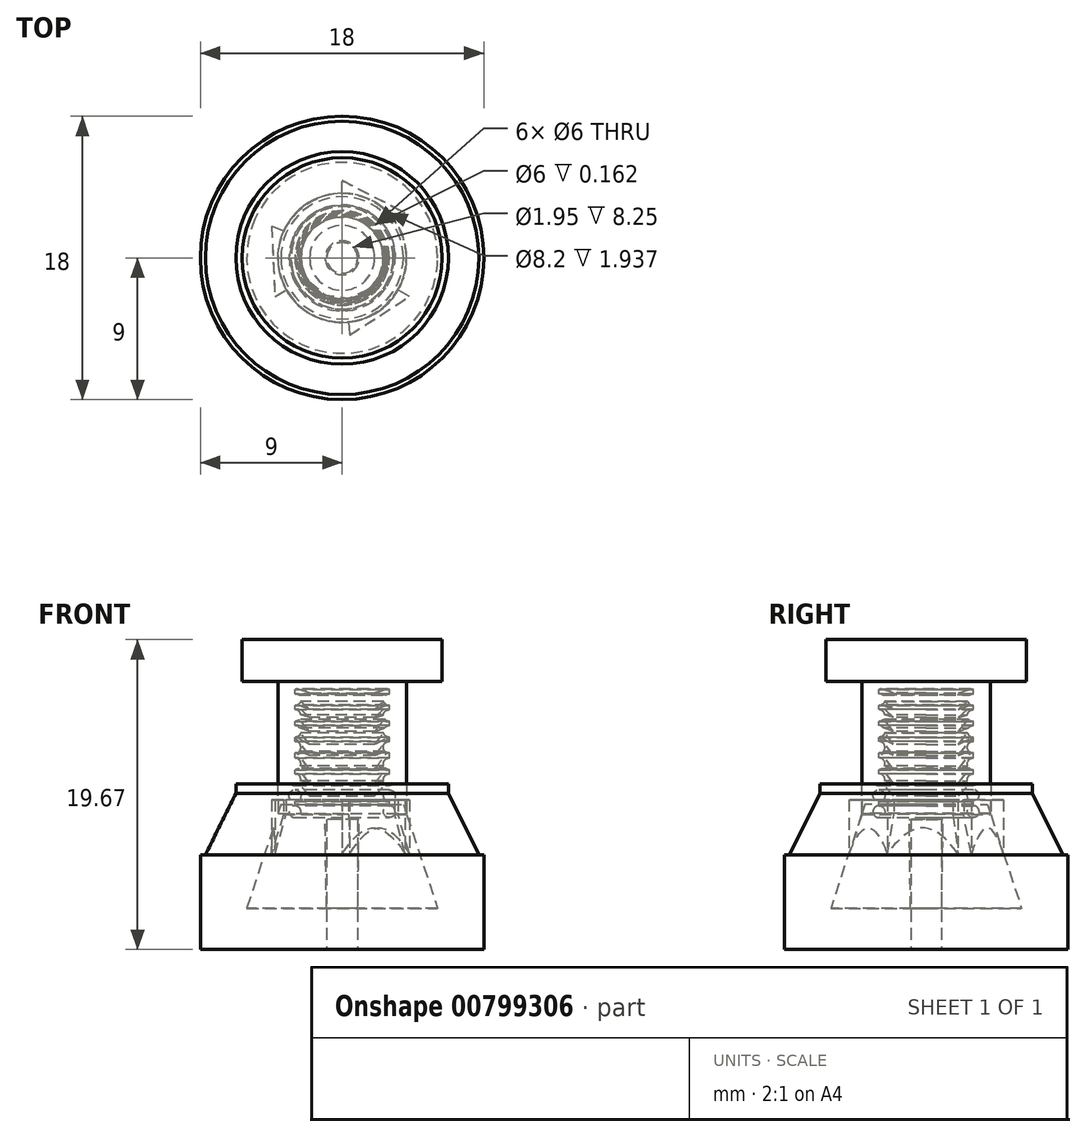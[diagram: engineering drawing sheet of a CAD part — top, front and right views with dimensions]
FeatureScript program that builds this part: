
annotation { "Feature Type Name" : "Feature", "Feature Type Description" : "" }
export const myFeature = defineFeature(function(context is Context, id is Id, definition is map)
    precondition{}
    {
        {
            var Q0;
            Q0=qCreatedBy(makeId("Top.planeOp"),FACE);
            var sketch = newSketch(context, id + "F0", { "sketchPlane" : qUnion([Q0])});
            skCircle(sketch, "E0", {"center": v(0, 0) * mm, "radius": 4.08 * mm});
            skSolve(sketch);
        }
        {
            var Q0;
            Q0=makeQuery(id+"F0.imprint","IMPRINT",FACE,{"disambiguationData":[TD([[makeQuery(id+"F0.imprint","IMPRINT",EDGE,{"derivedFrom":sQuery(id+"F0.wireOp",EDGE,"E0")}),1.0]])]});
            extrude(context, id + "F1", {"entities" : qUnion([Q0]), "depth" : 13 * mm, "offsetDistance" : 25 * mm});
        }
        {
            var Q0;
            Q0=qCreatedBy(makeId("Top.planeOp"),FACE);
            var sketch = newSketch(context, id + "F2", { "sketchPlane" : qUnion([Q0])});
            skCircle(sketch, "E1", {"center": v(0, 0) * mm, "radius": 9 * mm});
            skSolve(sketch);
        }
        {
            var Q0;
            Q0=makeQuery(id+"F2.imprint","IMPRINT",FACE,{"disambiguationData":[TD([[makeQuery(id+"F2.imprint","IMPRINT",EDGE,{"derivedFrom":sQuery(id+"F2.wireOp",EDGE,"E1")}),1.0]])]});
            extrude(context, id + "F3", {"entities" : qUnion([Q0]), "operationType" : NewBodyOperationType.ADD, "depth" : 3 * mm, "offsetDistance" : 25 * mm});
        }
        {
            var Q0;
            Q0=qCreatedBy(makeId("Top.planeOp"),FACE);
            var sketch = newSketch(context, id + "F4", { "sketchPlane" : qUnion([Q0])});
            skLineSegment(sketch, "E2", {"start": v(0, 0) * mm, "end": v(0, 10.37) * mm, "construction": true});
            skLineSegment(sketch, "E3", {"start": v(0, 0) * mm, "end": v(10.66, -6.15) * mm, "construction": true});
            skLineSegment(sketch, "E4", {"start": v(0, 0) * mm, "end": v(-9.47, -5.47) * mm, "construction": true});
            skCircle(sketch, "E5", {"center": v(0, 0) * mm, "radius": 4.92 * mm, "construction": true});
            skLineSegment(sketch, "E6", {"start": v(0, 0) * mm, "end": v(4, 2.87) * mm});
            skLineSegment(sketch, "E7", {"start": v(4, 2.87) * mm, "end": v(0, 4.92) * mm});
            skLineSegment(sketch, "E8", {"start": v(0, 4.92) * mm, "end": v(0, 0) * mm});
            skLineSegment(sketch, "E9", {"start": v(0, 0) * mm, "end": v(4.27, -2.46) * mm});
            skLineSegment(sketch, "E10", {"start": v(4.27, -2.46) * mm, "end": v(0.48, -4.9) * mm});
            skLineSegment(sketch, "E11", {"start": v(0.48, -4.9) * mm, "end": v(0, 0) * mm});
            skLineSegment(sketch, "E12", {"start": v(0, 0) * mm, "end": v(-4.27, -2.46) * mm});
            skLineSegment(sketch, "E13", {"start": v(-4.27, -2.46) * mm, "end": v(-4.49, 2.03) * mm});
            skLineSegment(sketch, "E14", {"start": v(-4.49, 2.03) * mm, "end": v(0, 0) * mm});
            skSolve(sketch);
        }
        {
            var Q0;
            Q0 = qSketchRegion(id + "F4", true);
            extrude(context, id + "F5", {"entities" : qUnion([Q0]), "operationType" : NewBodyOperationType.ADD, "depth" : 5 * mm, "offsetDistance" : 25 * mm});
        }
        {
            var Q0;
            Q0=qCreatedBy(makeId("Top.planeOp"),FACE);
            var sketch = newSketch(context, id + "F6", { "sketchPlane" : qUnion([Q0])});
            skCircle(sketch, "E15", {"center": v(0, 0) * mm, "radius": 0.97 * mm});
            skSolve(sketch);
        }
        {
            var Q0;
            Q0 = qSketchRegion(id + "F6", true);
            extrude(context, id + "F7", {"entities" : qUnion([Q0]), "operationType" : NewBodyOperationType.REMOVE, "endBound" : BoundingType.UP_TO_NEXT, "depth" : 25 * mm, "offsetDistance" : 25 * mm});
        }
        {
            var Q0;
            Q0=makeQuery(id+"F3.opExtrude","CAP_FACE",FACE,{"disambiguationData":[OSD([sQuery(id+"F2.wireOp",EDGE,"E1")])],"isStart":false});
            var sketch = newSketch(context, id + "F8", { "sketchPlane" : qUnion([Q0])});
            skCircle(sketch, "E16", {"center": v(0, 0) * mm, "radius": 9 * mm});
            skSolve(sketch);
        }
        {
            var Q0;
            Q0=makeQuery(id+"F8.imprint","IMPRINT",FACE,{"disambiguationData":[TD([[makeQuery(id+"F8.imprint","IMPRINT",EDGE,{"derivedFrom":sQuery(id+"F8.wireOp",EDGE,"E16")}),1.0]])]});
            extrude(context, id + "F9", {"entities" : qUnion([Q0]), "depth" : 3 * mm, "offsetDistance" : 25 * mm});
        }
        {
            var Q0;
            Q0=makeQuery(id+"F9.opExtrude","CAP_FACE",FACE,{"disambiguationData":[OSD([sQuery(id+"F0.wireOp",EDGE,"E0"),sQuery(id+"F2.wireOp",EDGE,"E1"),sQuery(id+"F4.wireOp",EDGE,"E6"),sQuery(id+"F4.wireOp",EDGE,"E7"),sQuery(id+"F4.wireOp",EDGE,"E8"),sQuery(id+"F4.wireOp",EDGE,"E9"),sQuery(id+"F4.wireOp",EDGE,"E10"),sQuery(id+"F4.wireOp",EDGE,"E11"),sQuery(id+"F4.wireOp",EDGE,"E12"),sQuery(id+"F4.wireOp",EDGE,"E13"),sQuery(id+"F4.wireOp",EDGE,"E14"),sQuery(id+"F8.wireOp",EDGE,"E16")])],"isStart":false});
            var sketch = newSketch(context, id + "F10", { "sketchPlane" : qUnion([Q0])});
            skCircle(sketch, "E17", {"center": v(0, 0) * mm, "radius": 6 * mm});
            skCircle(sketch, "E18", {"center": v(0, 0) * mm, "radius": 4.1 * mm});
            skSolve(sketch);
        }
        {
            var Q0;
            Q0=makeQuery(id+"F10.imprint","IMPRINT",FACE,{"disambiguationData":[TD([[makeQuery(id+"F10.imprint","IMPRINT",EDGE,{"derivedFrom":sQuery(id+"F10.wireOp",EDGE,"E17")}),1.0]])]});
            extrude(context, id + "F11", {"entities" : qUnion([Q0]), "operationType" : NewBodyOperationType.ADD, "depth" : 3.5 * mm, "offsetDistance" : 25 * mm});
        }
        {
            var Q0;
            Q0=makeQuery(id+"F11.opExtrude","CAP_FACE",FACE,{"disambiguationData":[OSD([sQuery(id+"F2.wireOp",EDGE,"E1"),sQuery(id+"F4.wireOp",EDGE,"E6"),sQuery(id+"F4.wireOp",EDGE,"E7"),sQuery(id+"F4.wireOp",EDGE,"E8"),sQuery(id+"F4.wireOp",EDGE,"E9"),sQuery(id+"F4.wireOp",EDGE,"E10"),sQuery(id+"F4.wireOp",EDGE,"E11"),sQuery(id+"F4.wireOp",EDGE,"E12"),sQuery(id+"F4.wireOp",EDGE,"E13"),sQuery(id+"F4.wireOp",EDGE,"E14"),sQuery(id+"F10.wireOp",EDGE,"E17"),sQuery(id+"F10.wireOp",EDGE,"E18")])],"isStart":false});
            var sketch = newSketch(context, id + "F12", { "sketchPlane" : qUnion([Q0])});
            skCircle(sketch, "E19", {"center": v(0, 0) * mm, "radius": 6.75 * mm});
            skSolve(sketch);
        }
        {
            var Q0;
            Q0 = qSketchRegion(id + "F12", true);
            extrude(context, id + "F13", {"entities" : qUnion([Q0]), "operationType" : NewBodyOperationType.ADD, "depth" : 1 * mm, "offsetDistance" : 25 * mm});
        }
        {
            var Q0;
            Q0=makeQuery(id+"F13.opExtrude","CAP_FACE",FACE,{"disambiguationData":[OSD([sQuery(id+"F12.wireOp",EDGE,"E19")])],"isStart":false});
            var sketch = newSketch(context, id + "F14", { "sketchPlane" : qUnion([Q0])});
            skCircle(sketch, "E20", {"center": v(0, 0) * mm, "radius": 4.1 * mm});
            skSolve(sketch);
        }
        {
            var Q0;
            Q0 = qSketchRegion(id + "F14", true);
            extrude(context, id + "F15", {"entities" : qUnion([Q0]), "operationType" : NewBodyOperationType.REMOVE, "oppositeDirection" : true, "depth" : 1 * mm, "offsetDistance" : 25 * mm});
        }
        {
            var Q0;
            Q0=qCreatedBy(makeId("Front.planeOp"),FACE);
            var sketch = newSketch(context, id + "F16", { "sketchPlane" : qUnion([Q0])});
            skLineSegment(sketch, "E21", {"start": v(0, 0) * mm, "end": v(0, 14.07) * mm, "construction": true});
            skLineSegment(sketch, "E22", {"start": v(-6.68, 10.05) * mm, "end": v(-8.74, 5.89) * mm});
            skLineSegment(sketch, "E23", {"start": v(-8.74, 5.89) * mm, "end": v(-5.87, 5.89) * mm});
            skLineSegment(sketch, "E24", {"start": v(-5.87, 5.89) * mm, "end": v(-5.87, 9.87) * mm});
            skLineSegment(sketch, "E25", {"start": v(-5.87, 9.87) * mm, "end": v(-6.68, 10.05) * mm});
            skSolve(sketch);
        }
        {
            var Q0;
            Q0=makeQuery(id+"F16.imprint","IMPRINT",FACE,{"disambiguationData":[TD([[makeQuery(id+"F16.imprint","IMPRINT",EDGE,{"derivedFrom":sQuery(id+"F16.wireOp",EDGE,"E22")}),1.0]])]});
            var Q1;
            Q1=sQuery(id+"F16.wireOp",EDGE,"E21");
            revolve(context, id + "F17", {"operationType" : NewBodyOperationType.ADD, "surfaceOperationType" : NewSurfaceOperationType.NEW, "entities" : qUnion([Q0]), "axis" : qUnion([Q1]), "revolveType" : RevolveType.FULL});
        }
        {
            var Q0;
            Q0=qCreatedBy(makeId("Front.planeOp"),FACE);
            var sketch = newSketch(context, id + "F18", { "sketchPlane" : qUnion([Q0])});
            skLineSegment(sketch, "E26", {"start": v(0, 0) * mm, "end": v(0, 10.64) * mm, "construction": true});
            skLineSegment(sketch, "E27", {"start": v(-3.88, 9.22) * mm, "end": v(-6.06, 2.61) * mm});
            skLineSegment(sketch, "E28", {"start": v(-6.06, 2.61) * mm, "end": v(-1, 2.61) * mm});
            skLineSegment(sketch, "E29", {"start": v(-1, 2.61) * mm, "end": v(-1.1, 9.22) * mm});
            skLineSegment(sketch, "E30", {"start": v(-1.1, 9.22) * mm, "end": v(-3.88, 9.22) * mm});
            skSolve(sketch);
        }
        {
            var Q0;
            Q0=makeQuery(id+"F18.imprint","IMPRINT",FACE,{"disambiguationData":[TD([[makeQuery(id+"F18.imprint","IMPRINT",EDGE,{"derivedFrom":sQuery(id+"F18.wireOp",EDGE,"E27")}),1.0]])]});
            var Q1;
            Q1=sQuery(id+"F18.wireOp",EDGE,"E26");
            revolve(context, id + "F19", {"operationType" : NewBodyOperationType.REMOVE, "surfaceOperationType" : NewSurfaceOperationType.NEW, "entities" : qUnion([Q0]), "axis" : qUnion([Q1]), "revolveType" : RevolveType.FULL, "oppositeDirection" : true});
        }
        {
            var Q0;
            Q0=makeQuery(id+"F1.opExtrude","CAP_FACE",FACE,{"disambiguationData":[OSD([sQuery(id+"F0.wireOp",EDGE,"E0")])],"isStart":false});
            var sketch = newSketch(context, id + "F20", { "sketchPlane" : qUnion([Q0])});
            skCircle(sketch, "E31", {"center": v(0, 0) * mm, "radius": 4.08 * mm});
            skSolve(sketch);
        }
        {
            var Q0;
            Q0 = qSketchRegion(id + "F20", true);
            extrude(context, id + "F21", {"entities" : qUnion([Q0]), "operationType" : NewBodyOperationType.ADD, "depth" : 4.25 * mm, "offsetDistance" : 25 * mm});
        }
        {
            var Q0;
            Q0=makeQuery(id+"F21.opExtrude","CAP_FACE",FACE,{"disambiguationData":[OSD([sQuery(id+"F20.wireOp",EDGE,"E31")])],"isStart":false});
            var sketch = newSketch(context, id + "F22", { "sketchPlane" : qUnion([Q0])});
            skCircle(sketch, "E32", {"center": v(0, 0) * mm, "radius": 3 * mm});
            skSolve(sketch);
        }
        {
            var Q0;
            Q0 = qSketchRegion(id + "F22", true);
            extrude(context, id + "F23", {"entities" : qUnion([Q0]), "operationType" : NewBodyOperationType.REMOVE, "oppositeDirection" : true, "depth" : 9 * mm, "offsetDistance" : 25 * mm});
        }
        {
            var Q0;
            Q0=qCreatedBy(makeId("Front.planeOp"),FACE);
            var sketch = newSketch(context, id + "F24", { "sketchPlane" : qUnion([Q0])});
            skLineSegment(sketch, "E33", {"start": v(0, 5.73) * mm, "end": v(0, 20.07) * mm, "construction": true});
            skLineSegment(sketch, "E34", {"start": v(1.15, 17.03) * mm, "end": v(-8.67, 17.03) * mm, "construction": true});
            skLineSegment(sketch, "E35", {"start": v(-3, 9.08) * mm, "end": v(-3, 20.34) * mm, "construction": true});
            skLineSegment(sketch, "E36", {"start": v(-2.06, 20.34) * mm, "end": v(-2.06, 7.32) * mm, "construction": true});
            skLineSegment(sketch, "E37", {"start": v(-6.35, 17.03) * mm, "end": v(-6.35, 19.67) * mm});
            skLineSegment(sketch, "E38", {"start": v(-6.35, 19.67) * mm, "end": v(0, 19.67) * mm});
            skLineSegment(sketch, "E39", {"start": v(0, 19.67) * mm, "end": v(0, 9.73) * mm});
            skLineSegment(sketch, "E40", {"start": v(0, 9.73) * mm, "end": v(-2.06, 9.73) * mm});
            skLineSegment(sketch, "E41", {"start": v(-2.06, 9.73) * mm, "end": v(-3, 10.8) * mm});
            skLineSegment(sketch, "E42", {"start": v(-3, 10.8) * mm, "end": v(-2.06, 10.53) * mm});
            skLineSegment(sketch, "E43", {"start": v(-2.06, 10.53) * mm, "end": v(-3, 11.8) * mm});
            skLineSegment(sketch, "E44", {"start": v(-3, 11.8) * mm, "end": v(-2.06, 11.43) * mm});
            skLineSegment(sketch, "E45", {"start": v(-2.06, 11.43) * mm, "end": v(-3, 12.7) * mm});
            skLineSegment(sketch, "E46", {"start": v(-3, 12.7) * mm, "end": v(-2.06, 12.33) * mm});
            skLineSegment(sketch, "E47", {"start": v(-2.06, 12.33) * mm, "end": v(-3, 13.5) * mm});
            skLineSegment(sketch, "E48", {"start": v(-3, 13.5) * mm, "end": v(-2.06, 13.03) * mm});
            skLineSegment(sketch, "E49", {"start": v(-2.06, 13.03) * mm, "end": v(-3, 14.2) * mm});
            skLineSegment(sketch, "E50", {"start": v(-3, 14.2) * mm, "end": v(-2.06, 13.83) * mm});
            skLineSegment(sketch, "E51", {"start": v(-2.06, 13.83) * mm, "end": v(-3, 15) * mm});
            skLineSegment(sketch, "E52", {"start": v(-3, 15) * mm, "end": v(-2.06, 14.73) * mm});
            skLineSegment(sketch, "E53", {"start": v(-2.06, 14.73) * mm, "end": v(-3, 15.6) * mm});
            skLineSegment(sketch, "E54", {"start": v(-3, 15.6) * mm, "end": v(-2.06, 15.23) * mm});
            skLineSegment(sketch, "E55", {"start": v(-2.06, 15.23) * mm, "end": v(-3, 16.1) * mm});
            skLineSegment(sketch, "E56", {"start": v(-3, 16.1) * mm, "end": v(-2.06, 16.3) * mm});
            skLineSegment(sketch, "E57", {"start": v(-2.06, 16.3) * mm, "end": v(-3, 16.6) * mm});
            skLineSegment(sketch, "E58", {"start": v(-2.8, 17.03) * mm, "end": v(-6.35, 17.03) * mm});
            skLineSegment(sketch, "E59", {"start": v(-3, 16.6) * mm, "end": v(-2.8, 17.03) * mm});
            skSolve(sketch);
        }
        {
            var Q0;
            Q0 = qSketchRegion(id + "F24", true);
            var Q1;
            Q1=sQuery(id+"F24.wireOp",EDGE,"E33");
            revolve(context, id + "F25", {"surfaceOperationType" : NewSurfaceOperationType.NEW, "entities" : qUnion([Q0]), "axis" : qUnion([Q1]), "revolveType" : RevolveType.FULL});
        }
        {
            var Q0;
            Q0=qCreatedBy(makeId("Front.planeOp"),FACE);
            var sketch = newSketch(context, id + "F26", { "sketchPlane" : qUnion([Q0])});
            skLineSegment(sketch, "E60", {"start": v(0, 0) * mm, "end": v(0, 18) * mm, "construction": true});
            skLineSegment(sketch, "E61", {"start": v(-3, 17.26) * mm, "end": v(-3, 7.36) * mm, "construction": true});
            skCircle(sketch, "E62", {"center": v(-3, 16.88) * mm, "radius": 0.38 * mm});
            skCircle(sketch, "E63", {"center": v(-3, 15.86) * mm, "radius": 0.38 * mm});
            skCircle(sketch, "E64", {"center": v(-3, 13.84) * mm, "radius": 0.38 * mm});
            skCircle(sketch, "E65", {"center": v(-3, 12.84) * mm, "radius": 0.38 * mm});
            skCircle(sketch, "E66", {"center": v(-3, 14.85) * mm, "radius": 0.38 * mm});
            skPoint(sketch, "E67", {"position": v(-3, 12.3) * mm});
            skCircle(sketch, "E68", {"center": v(-3, 11.78) * mm, "radius": 0.38 * mm});
            skCircle(sketch, "E69", {"center": v(-3, 10.78) * mm, "radius": 0.38 * mm});
            skCircle(sketch, "E70", {"center": v(-3, 9.76) * mm, "radius": 0.38 * mm});
            skCircle(sketch, "E71", {"center": v(-3, 8.74) * mm, "radius": 0.38 * mm});
            skSolve(sketch);
        }
        {
            var Q0;
            Q0 = qSketchRegion(id + "F26", true);
            var Q1;
            Q1=sQuery(id+"F26.wireOp",EDGE,"E60");
            revolve(context, id + "F27", {"operationType" : NewBodyOperationType.ADD, "surfaceOperationType" : NewSurfaceOperationType.NEW, "entities" : qUnion([Q0]), "axis" : qUnion([Q1]), "revolveType" : RevolveType.FULL});
        }
    });
